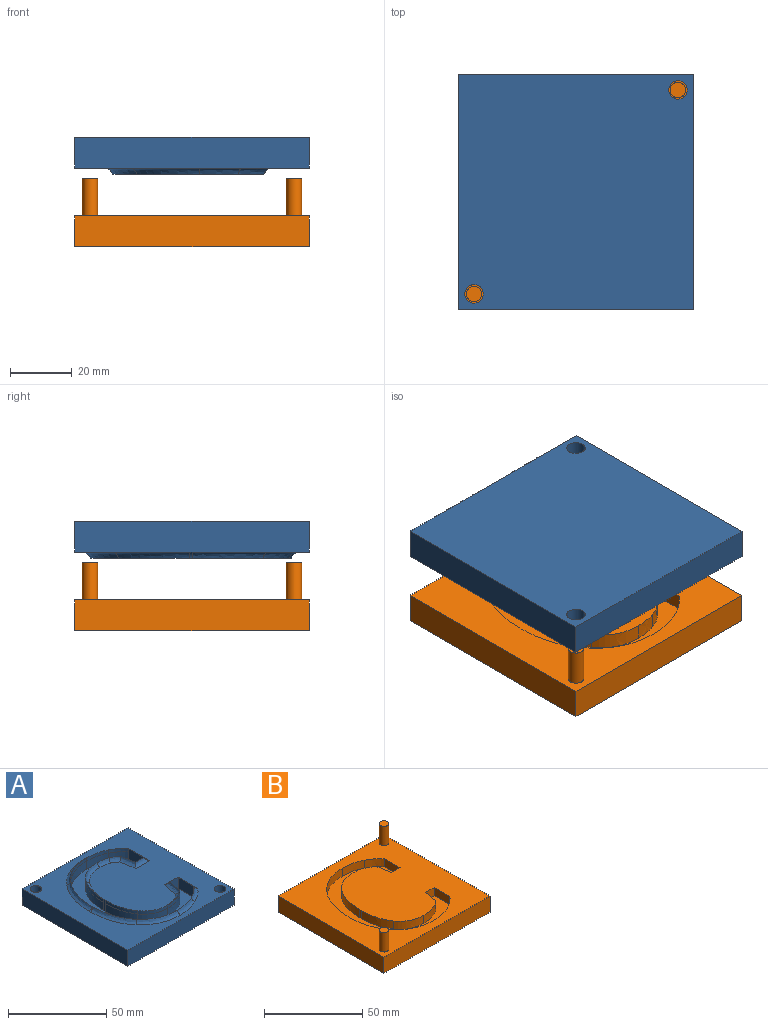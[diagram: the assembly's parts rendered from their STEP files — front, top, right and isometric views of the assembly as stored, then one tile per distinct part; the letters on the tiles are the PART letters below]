
ASSEMBLY  parts=2 mates=1
PART A: 73 faces, bbox 76.3x76.3x12.1 mm
  f0: plane 76.26x76.26mm, normal (0,0,1), area 4081.4mm2, adj f1,f2,f3,f4,f6,f7,f9,f11
  f1: plane 76.2x10mm, normal (0,1,0), area 762mm2, adj f0,f2,f4,f5
  f2: plane 76.2x10mm, normal (-1,0,0), area 762mm2, adj f0,f1,f3,f5
  f3: plane 76.2x10mm, normal (0,-1,0), area 762mm2, adj f0,f2,f4,f5
  f4: plane 76.2x10mm, normal (1,0,0), area 762mm2, adj f0,f1,f3,f5
  f5: plane 76.2x76.2mm, normal (0,0,-1), area 5749.9mm2, adj f1,f2,f3,f4,f71,f72
  f6: bspline ~11.24x3.93mm, area 28.1mm2, adj f0,f7,f24,f68
  f7: bspline ~10.29x2mm, area 22.8mm2, adj f0,f6,f25,f69
  f8: bspline ~5.44x3.31mm, area 12.8mm2, adj f9,f10,f58,f59
  f9: bspline ~6.15x4.7mm, area 16.8mm2, adj f0,f8,f11,f26
  f10: bspline ~7.84x2mm, area 16mm2, adj f8,f11,f12,f60
  f11: bspline ~7.84x3.21mm, area 22.5mm2, adj f0,f9,f10,f13
  f12: bspline ~14.44x7.2mm, area 33.6mm2, adj f10,f13,f14,f61
  f13: bspline ~14.44x8.37mm, area 46.8mm2, adj f0,f11,f12,f15
  f14: bspline ~18.23x5.2mm, area 38.5mm2, adj f12,f15,f62,f63
  f15: bspline ~18.23x6.82mm, area 54.8mm2, adj f0,f13,f14,f16
  f16: bspline ~2x2mm, area 2.9mm2, adj f0,f15,f18,f63
  f17: bspline ~18.17x5.31mm, area 38.5mm2, adj f18,f19,f63,f64
  f18: bspline ~18.17x6.92mm, area 54.7mm2, adj f0,f16,f17,f20
  f19: bspline ~15.19x7.16mm, area 34.9mm2, adj f17,f20,f21,f65
  f20: bspline ~15.19x8.35mm, area 48.8mm2, adj f0,f18,f19,f22
  f21: bspline ~7.28x2mm, area 14.9mm2, adj f19,f22,f23,f66
  f22: bspline ~7.28x3.14mm, area 20.8mm2, adj f0,f20,f21,f24
  f23: bspline ~5.14x3.35mm, area 12.3mm2, adj f21,f24,f67,f68
  f24: bspline ~5.92x4.78mm, area 16.2mm2, adj f0,f6,f22,f23
  f25: bspline ~14.45x2mm, area 36.7mm2, adj f0,f7,f28,f70
  f26: bspline ~10.97x3.88mm, area 28.1mm2, adj f0,f9,f44,f58
  f27: bspline ~8.23x6.29mm, area 20.9mm2, adj f28,f29,f47,f70
  f28: bspline ~10.33x8.75mm, area 32.5mm2, adj f0,f25,f27,f30
  f29: bspline ~12.72x2.81mm, area 26.3mm2, adj f27,f30,f31,f48
  f30: bspline ~13.63x4.81mm, area 39.6mm2, adj f0,f28,f29,f32
  f31: bspline ~20.42x9.13mm, area 46.3mm2, adj f29,f32,f33,f49
  f32: bspline ~21.94x11.13mm, area 69.8mm2, adj f0,f30,f31,f34
  f33: bspline ~23.06x7.8mm, area 49.8mm2, adj f31,f34,f50,f51
  f34: bspline ~24.36x9.8mm, area 74.5mm2, adj f0,f32,f33,f35
  f35: bspline ~2x2mm, area 2.6mm2, adj f0,f34,f37,f51
  f36: bspline ~23x7.92mm, area 49.7mm2, adj f37,f38,f51,f52
  f37: bspline ~24.31x9.92mm, area 74.5mm2, adj f0,f35,f36,f39
  f38: bspline ~20.3x9.15mm, area 46mm2, adj f36,f39,f40,f53
  f39: bspline ~21.81x11.15mm, area 69.4mm2, adj f0,f37,f38,f41
  f40: bspline ~12.72x2.77mm, area 26.3mm2, adj f38,f41,f42,f54
  f41: bspline ~13.62x4.77mm, area 39.6mm2, adj f0,f39,f40,f43
  f42: bspline ~8.23x6.29mm, area 20.9mm2, adj f40,f43,f55,f56
  f43: bspline ~10.33x8.75mm, area 32.6mm2, adj f0,f41,f42,f45
  f44: bspline ~10.29x2mm, area 22.8mm2, adj f0,f26,f45,f57
  f45: bspline ~14.44x2mm, area 36.7mm2, adj f0,f43,f44,f56
  f46: plane 65.24x49.16mm, normal (0,0,1), area 1056mm2, adj f47,f48,f49,f50,f51,f52,f53,f54
  f47: extruded ~8.23x6.29mm, area 52.2mm2, adj f27,f46,f48,f70
  f48: extruded ~12.72x5mm, area 65.7mm2, adj f29,f46,f47,f49
  f49: extruded ~20.42x9.13mm, area 115.7mm2, adj f31,f46,f48,f50
  f50: extruded ~23.06x7.8mm, area 124.4mm2, adj f33,f46,f49,f51
  f51: plane 7x0.91mm, normal (1,0,0), area 6.3mm2, adj f33,f35,f36,f46,f50,f52
  f52: extruded ~23x7.92mm, area 124.4mm2, adj f36,f46,f51,f53
  f53: extruded ~20.3x9.15mm, area 115.1mm2, adj f38,f46,f52,f54
  f54: extruded ~12.72x5mm, area 65.7mm2, adj f40,f46,f53,f55
  f55: extruded ~8.23x6.29mm, area 52.2mm2, adj f42,f46,f54,f56
  f56: plane 11.29x7mm, normal (-1,0,0), area 79mm2, adj f42,f45,f46,f55,f57
  f57: plane 7x6.05mm, normal (0,-1,0), area 42.3mm2, adj f44,f46,f56,f58
  f58: plane 8.97x7mm, normal (0.98,-0.18,0), area 63.8mm2, adj f8,f26,f46,f57,f59
  f59: extruded ~5.44x5mm, area 32.1mm2, adj f8,f46,f58,f60
  f60: extruded ~7.84x5mm, area 40mm2, adj f10,f46,f59,f61
  f61: extruded ~14.44x7.2mm, area 84.1mm2, adj f12,f46,f60,f62
  f62: extruded ~18.23x5.2mm, area 96.4mm2, adj f14,f46,f61,f63
  f63: plane 7x1mm, normal (-1,0,0), area 7mm2, adj f14,f16,f17,f46,f62,f64
  f64: extruded ~18.17x5.31mm, area 96.3mm2, adj f17,f46,f63,f65
  f65: extruded ~15.19x7.16mm, area 87.4mm2, adj f19,f46,f64,f66
  f66: extruded ~7.28x5mm, area 37.2mm2, adj f21,f46,f65,f67
  f67: extruded ~5.14x5mm, area 30.8mm2, adj f23,f46,f66,f68
  f68: plane 8.97x7mm, normal (0.98,0.18,0), area 63.8mm2, adj f6,f23,f46,f67,f69
  f69: plane 7x6.05mm, normal (0,1,0), area 42.3mm2, adj f7,f46,f68,f70
  f70: plane 11.29x7mm, normal (-1,0,0), area 79mm2, adj f25,f27,f46,f47,f69
  f71: cylinder r=3mm len=10mm, axis (0,0,1), area 188.5mm2, adj f0,f5
  f72: cylinder r=3mm len=10mm, axis (0,0,1), area 188.5mm2, adj f0,f5
PART B: 35 faces, bbox 76.2x76.2x22 mm
  f0: plane 76.2x76.2mm, normal (0,0,1), area 4711.2mm2, adj f1,f2,f3,f4,f6,f7,f8,f9
  f1: plane 76.2x10mm, normal (0,1,0), area 762mm2, adj f0,f2,f4,f5
  f2: plane 76.2x10mm, normal (-1,0,0), area 762mm2, adj f0,f1,f3,f5
  f3: plane 76.2x10mm, normal (0,-1,0), area 762mm2, adj f0,f2,f4,f5
  f4: plane 76.2x10mm, normal (1,0,0), area 762mm2, adj f0,f1,f3,f5
  f5: plane 76.2x76.2mm, normal (0,0,-1), area 5806.4mm2, adj f1,f2,f3,f4
  f6: plane 6.05x5mm, normal (0,1,0), area 30.2mm2, adj f0,f7,f29,f30
  f7: plane 11.29x5mm, normal (-1,0,0), area 56.4mm2, adj f0,f6,f8,f30
  f8: extruded ~8.23x6.29mm, area 52.2mm2, adj f0,f7,f9,f30
  f9: extruded ~12.72x5mm, area 65.7mm2, adj f0,f8,f10,f30
  f10: extruded ~20.42x9.13mm, area 115.7mm2, adj f0,f9,f11,f30
  f11: extruded ~23.06x7.8mm, area 124.4mm2, adj f0,f10,f12,f30
  f12: plane 5x0.91mm, normal (1,0,0), area 4.5mm2, adj f0,f11,f13,f30
  f13: extruded ~23x7.92mm, area 124.4mm2, adj f0,f12,f14,f30
  f14: extruded ~20.3x9.15mm, area 115.1mm2, adj f0,f13,f15,f30
  f15: extruded ~12.72x5mm, area 65.7mm2, adj f0,f14,f16,f30
  f16: extruded ~8.23x6.29mm, area 52.2mm2, adj f0,f15,f17,f30
  f17: plane 11.29x5mm, normal (-1,0,0), area 56.4mm2, adj f0,f16,f18,f30
  f18: plane 6.05x5mm, normal (0,-1,0), area 30.2mm2, adj f0,f17,f19,f30
  f19: plane 8.97x5mm, normal (0.98,-0.18,0), area 45.6mm2, adj f0,f18,f20,f30
  f20: extruded ~5.44x5mm, area 32.1mm2, adj f0,f19,f21,f30
  f21: extruded ~7.84x5mm, area 40mm2, adj f0,f20,f22,f30
  f22: extruded ~14.44x7.2mm, area 84.1mm2, adj f0,f21,f23,f30
  f23: extruded ~18.23x5.2mm, area 96.4mm2, adj f0,f22,f24,f30
  f24: plane 5x1mm, normal (-1,0,0), area 5mm2, adj f0,f23,f25,f30
  f25: extruded ~18.17x5.31mm, area 96.3mm2, adj f0,f24,f26,f30
  f26: extruded ~15.19x7.16mm, area 87.4mm2, adj f0,f25,f27,f30
  f27: extruded ~7.28x5mm, area 37.2mm2, adj f0,f26,f28,f30
  f28: extruded ~5.14x5mm, area 30.8mm2, adj f0,f27,f29,f30
  f29: plane 8.97x5mm, normal (0.98,0.18,0), area 45.6mm2, adj f0,f6,f28,f30
  f30: plane 65.24x49.16mm, normal (0,0,1), area 1056mm2, adj f6,f7,f8,f9,f10,f11,f12,f13
  f31: cylinder r=2.5mm len=12mm, axis (0,0,-1), area 188.5mm2, adj f0,f32
  f32: plane 5x5mm, normal (0,0,1), area 19.6mm2, adj f31
  f33: cylinder r=2.5mm len=12mm, axis (0,0,-1), area 188.5mm2, adj f0,f34
  f34: plane 5x5mm, normal (0,0,1), area 19.6mm2, adj f33
PLACE A rot(axis=(1,0,0),180deg) t=(-38.1,38.1,35.53)mm
PLACE B t=(-38.1,38.1,0)mm
MATE slider A.f0 <-> B.f0  axis (0,0,-1) through (0,76.2,25.53)mm
